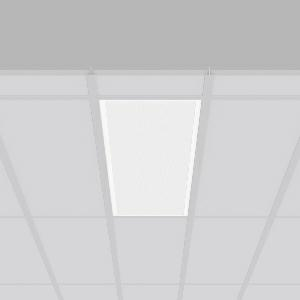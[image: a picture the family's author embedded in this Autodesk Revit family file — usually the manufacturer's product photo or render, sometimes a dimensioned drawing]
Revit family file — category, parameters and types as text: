
# Revit family: sidelite_eco_672368_002_1_07_2839
name_source: partatom
category: Lighting Fixtures
units: mm (PartAtom-declared; Revit-internal decimal feet)

## family parameters
Cut with Voids When Loaded = No
Host = Face
Light Source = No
Part Type = Normal
Room Calculation Point = No
Round Connector Dimension = Use Diameter
Shared = No

## types (1)
- SIDELITE ECO (1 x LED Modul 840, 3450 lm, 4000)
    Apparent Load = 29 VA
    CIE Flux Codes = 59 87 97 100 100
    Color Rendering = 80
    Color Temperature = 4000
    Default Elevation = 1800 mm
    Description = Series: SIDELITE ECO
Highly economical recessed luminaire with progressive LED technology. For escape route illumination. Frame made of aluminium, powder-coated. Diffuser plastic microprismatic. Lightguide and diffuser made of non-yellowing plastic (PMMA). Lateral light emission (RZB SIDELITE technology) for homogeneous light distribution. External driver. Self-contained system with automatic self-test and feedback via DALI bus, only to RZB DALI monitoring system. External driver with simple plug-in locking system. Extended connection cable (1.90 m). 
Colour: white
Length: 1195 mm
Width: 295 mm
Cut-out length: 1170 mm
Cut-out width: 270 mm
Recess height: 160 mm
Luminaire: recess height: 40 mm
Weight: 4.4 kg
Operating mode: maintained power mode
Duration time: 3 h
Lamp: LED
Socket: without socket
Colour temperature: 4000K
Colour rendering index (CRI): 80
System power: 29 W
Rated luminous flux: 3450 lm
Luminous flux, emergency: 510 lm
System power, emergency: -
Control gear: Regulated power supply
Protection class: I
Type of protection: IP 40
    Height = 0 mm  [stored 0 ft]
    Lamp = 1 x LED Modul 840
    Lamp Light Flux = 3450 lm
    Lamp count = 1
    Length = 1195 mm
    Lifetime = 50000 h
    Luminous efficacy = 119 lm/W
    Manufacturer = RZB
    ModVariant = No
    Model = 672368.002.1.07
    Mounting Place = Ceiling
    Mounting Type = Recessed
    Number of Poles = 1
    OnlyDefault = Yes
    Power Factor = 1
    Product Name = SIDELITE ECO
    Product group = Recessed modular luminaires
    ProductGroupID = 406
    Protection Class = Protection class I
    Protection Degree = IP 40
    RLX_Detail_Level = 1
    RLX_Emergency_Light_Flux = 510 lm
    RLX_Emergency_Type = 3
    RLX_Emergency_Type_DB = Yes
    RlxData = <blob elided: 34729 chars, md5=0586c6b3>
    Socket = socket
    Standby Power = 0 W
    System Light Flux = 3450 lm
    System Power = 29 W
    Type Comments = Product without accessories
    Type Image = 312366.002.jpg
    URL = http://relux.com
    VarID = ---
    Voltage = 230 V
    Voltage Range = 220-240 V
    Weight = 0.00 kg
    Width = 295 mm

note: [stored X ft] marks values corroborated as IEEE doubles in the binary element streams (Revit-internal decimal feet)

## geometry (parser evidence)
native form markers: Blend x4, Sweep x11
no freeform markers — native parametric forms only
